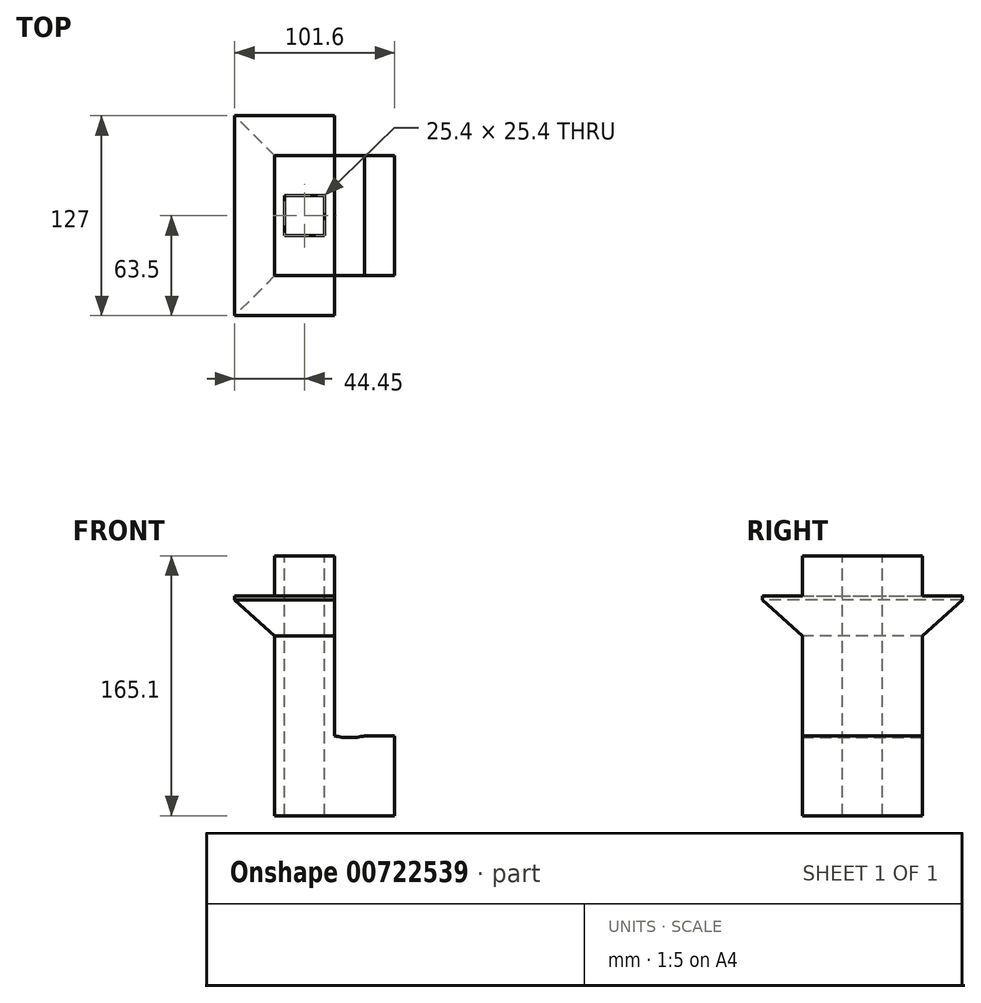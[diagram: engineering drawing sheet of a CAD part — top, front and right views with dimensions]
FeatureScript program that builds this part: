
annotation { "Feature Type Name" : "Feature", "Feature Type Description" : "" }
export const myFeature = defineFeature(function(context is Context, id is Id, definition is map)
    precondition{}
    {
        {
            var Q0;
            Q0=qCreatedBy(makeId("Top.planeOp"),FACE);
            var sketch = newSketch(context, id + "F0", { "sketchPlane" : qUnion([Q0])});
            skLineSegment(sketch, "E0.bottom", {"start": v(19.05, -38.1) * mm, "end": v(-19.05, -38.1) * mm});
            skLineSegment(sketch, "E0.top", {"start": v(19.05, 38.1) * mm, "end": v(-19.05, 38.1) * mm});
            skLineSegment(sketch, "E0.left", {"start": v(19.05, -38.1) * mm, "end": v(19.05, 38.1) * mm});
            skLineSegment(sketch, "E0.right", {"start": v(-19.05, -38.1) * mm, "end": v(-19.05, 38.1) * mm});
            skPoint(sketch, "E0.middle", {"position": v(0, 0) * mm});
            skSolve(sketch);
        }
        {
            var Q0;
            Q0=makeQuery(id+"F0.imprint","IMPRINT",FACE,{"disambiguationData":[TD([[makeQuery(id+"F0.imprint","IMPRINT",EDGE,{"derivedFrom":sQuery(id+"F0.wireOp",EDGE,"E0.bottom")}),-1.0]])]});
            extrude(context, id + "F1", {"entities" : qUnion([Q0]), "depth" : 177.8 * mm, "offsetDistance" : 25.4 * mm});
        }
        {
            var Q0;
            Q0=makeQuery(id+"F1.opExtrude","SWEPT_FACE",FACE,{"disambiguationData":[OSD([sQuery(id+"F0.wireOp",EDGE,"E0.right")])]});
            var sketch = newSketch(context, id + "F2", { "sketchPlane" : qUnion([Q0])});
            skLineSegment(sketch, "E1", {"start": v(38.1, 139.7) * mm, "end": v(-38.1, 139.7) * mm});
            skLineSegment(sketch, "E2", {"start": v(-38.1, 139.7) * mm, "end": v(-38.1, 114.3) * mm});
            skLineSegment(sketch, "E3", {"start": v(-38.1, 114.3) * mm, "end": v(38.1, 114.3) * mm});
            skLineSegment(sketch, "E4", {"start": v(38.1, 114.3) * mm, "end": v(38.1, 139.7) * mm});
            skSolve(sketch);
        }
        {
            var Q0;
            Q0=makeQuery(id+"F2.imprint","IMPRINT",FACE,{"disambiguationData":[TD([[makeQuery(id+"F2.imprint","IMPRINT",EDGE,{"derivedFrom":sQuery(id+"F2.wireOp",EDGE,"E1")}),1.0]])]});
            extrude(context, id + "F3", {"entities" : qUnion([Q0]), "operationType" : NewBodyOperationType.ADD, "depth" : 25.4 * mm, "offsetDistance" : 25.4 * mm});
        }
        {
            var Q0;
            Q0=makeQuery(id+"F3.boolean.opBoolean","MERGE",FACE,{"derivedFrom":[makeQuery(id+"F1.opExtrude","SWEPT_FACE",FACE,{"disambiguationData":[OSD([sQuery(id+"F0.wireOp",EDGE,"E0.bottom")])]}),makeQuery(id+"F3.opExtrude","SWEPT_FACE",FACE,{"disambiguationData":[OSD([sQuery(id+"F2.wireOp",EDGE,"E4")])]})]});
            var sketch = newSketch(context, id + "F4", { "sketchPlane" : qUnion([Q0])});
            skLineSegment(sketch, "E5", {"start": v(-63.5, 114.3) * mm, "end": v(19.05, 114.3) * mm});
            skLineSegment(sketch, "E6", {"start": v(19.05, 114.3) * mm, "end": v(19.05, 139.7) * mm});
            skLineSegment(sketch, "E7", {"start": v(19.05, 139.7) * mm, "end": v(-44.45, 139.7) * mm});
            skSolve(sketch);
        }
        {
            var Q0;
            {var subQ11=sQuery(id+"F4.wireOp",EDGE,"E6");Q0=makeQuery(id+"F4.imprint","IMPRINT",FACE,{"disambiguationData":[TD([[makeQuery(id+"F4.imprint","IMPRINT",EDGE,{"derivedFrom":subQ11}),-1.0]])]});}
            extrude(context, id + "F5", {"entities" : qUnion([Q0]), "operationType" : NewBodyOperationType.ADD, "depth" : 25.4 * mm, "offsetDistance" : 25.4 * mm});
        }
        {
            var Q0;
            Q0=makeQuery(id+"F3.boolean.opBoolean","MERGE",FACE,{"derivedFrom":[makeQuery(id+"F1.opExtrude","SWEPT_FACE",FACE,{"disambiguationData":[OSD([sQuery(id+"F0.wireOp",EDGE,"E0.top")])]}),makeQuery(id+"F3.opExtrude","SWEPT_FACE",FACE,{"disambiguationData":[OSD([sQuery(id+"F2.wireOp",EDGE,"E2")])]})]});
            var sketch = newSketch(context, id + "F6", { "sketchPlane" : qUnion([Q0])});
            skLineSegment(sketch, "E8", {"start": v(44.45, 139.7) * mm, "end": v(-19.05, 139.7) * mm});
            skLineSegment(sketch, "E9", {"start": v(-19.05, 139.7) * mm, "end": v(-19.05, 114.3) * mm});
            skLineSegment(sketch, "E10", {"start": v(-19.05, 114.3) * mm, "end": v(44.45, 114.3) * mm});
            skSolve(sketch);
        }
        {
            var Q0;
            Q0=qSketchRegion(id+"F6",true);
            var Q1;
            {var subQ11=sQuery(id+"F6.wireOp",EDGE,"E9");Q1=makeQuery(id+"F6.imprint","IMPRINT",FACE,{"disambiguationData":[TD([[makeQuery(id+"F6.imprint","IMPRINT",EDGE,{"derivedFrom":subQ11}),1.0]])]});}
            extrude(context, id + "F7", {"entities" : qUnion([Q0, Q1]), "operationType" : NewBodyOperationType.ADD, "depth" : 25.4 * mm, "offsetDistance" : 25.4 * mm});
        }
        {
            var Q0;
            Q0=makeQuery(id+"F7.boolean.opBoolean","MERGE",FACE,{"derivedFrom":[makeQuery(id+"F5.boolean.opBoolean","MERGE",FACE,{"derivedFrom":[makeQuery(id+"F1.opExtrude","SWEPT_FACE",FACE,{"disambiguationData":[OSD([sQuery(id+"F0.wireOp",EDGE,"E0.left")])]}),makeQuery(id+"F5.opExtrude","SWEPT_FACE",FACE,{"disambiguationData":[OSD([sQuery(id+"F4.wireOp",EDGE,"E6")])]})]}),makeQuery(id+"F7.opExtrude","SWEPT_FACE",FACE,{"disambiguationData":[OSD([sQuery(id+"F6.wireOp",EDGE,"E9")])]})]});
            var sketch = newSketch(context, id + "F8", { "sketchPlane" : qUnion([Q0])});
            skLineSegment(sketch, "E11", {"start": v(-63.5, 139.7) * mm, "end": v(-63.5, 137.16) * mm});
            skLineSegment(sketch, "E12", {"start": v(-63.5, 137.16) * mm, "end": v(-38.1, 114.3) * mm});
            skLineSegment(sketch, "E13", {"start": v(63.5, 139.7) * mm, "end": v(63.5, 137.16) * mm});
            skLineSegment(sketch, "E14", {"start": v(63.5, 137.16) * mm, "end": v(38.1, 114.3) * mm});
            skSolve(sketch);
        }
        {
            var Q0;
            Q0=qSketchRegion(id+"F8",true);
            var Q1;
            {var subQ0=sQuery(id+"F8.wireOp",EDGE,"E12");Q1=makeQuery(id+"F8.imprint","IMPRINT",FACE,{"disambiguationData":[TD([[makeQuery(id+"F8.imprint","IMPRINT",EDGE,{"derivedFrom":subQ0}),-1.0]])]});}
            var Q2;
            {var subQ0=sQuery(id+"F8.wireOp",EDGE,"E14");Q2=makeQuery(id+"F8.imprint","IMPRINT",FACE,{"disambiguationData":[TD([[makeQuery(id+"F8.imprint","IMPRINT",EDGE,{"derivedFrom":subQ0}),1.0]])]});}
            extrude(context, id + "F9", {"entities" : qUnion([Q0, Q1, Q2]), "operationType" : NewBodyOperationType.REMOVE, "oppositeDirection" : true, "depth" : 228.6 * mm, "offsetDistance" : 25.4 * mm});
        }
        {
            var Q0;
            Q0=makeQuery(id+"F5.opExtrude","CAP_FACE",FACE,{"disambiguationData":[OSD([sQuery(id+"F2.wireOp",EDGE,"E4"),sQuery(id+"F4.wireOp",EDGE,"E5"),sQuery(id+"F4.wireOp",EDGE,"E6"),sQuery(id+"F4.wireOp",EDGE,"E7")])],"isStart":false});
            var sketch = newSketch(context, id + "F10", { "sketchPlane" : qUnion([Q0])});
            skLineSegment(sketch, "E15", {"start": v(-44.45, 139.7) * mm, "end": v(-44.45, 137.16) * mm});
            skLineSegment(sketch, "E16", {"start": v(-44.45, 139.7) * mm, "end": v(-19.05, 139.7) * mm});
            skLineSegment(sketch, "E17", {"start": v(-19.05, 139.7) * mm, "end": v(-19.05, 114.3) * mm});
            skLineSegment(sketch, "E18", {"start": v(-19.05, 114.3) * mm, "end": v(-44.45, 137.16) * mm});
            skLineSegment(sketch, "E19", {"start": v(-44.45, 137.16) * mm, "end": v(-44.45, 114.3) * mm});
            skLineSegment(sketch, "E20", {"start": v(-44.45, 114.3) * mm, "end": v(-19.05, 114.3) * mm});
            skSolve(sketch);
        }
        {
            var Q0;
            Q0=makeQuery(id+"F10.imprint","IMPRINT",FACE,{"disambiguationData":[TD([[makeQuery(id+"F10.imprint","IMPRINT",EDGE,{"derivedFrom":sQuery(id+"F10.wireOp",EDGE,"E18")}),1.0]])]});
            extrude(context, id + "F11", {"entities" : qUnion([Q0]), "operationType" : NewBodyOperationType.REMOVE, "oppositeDirection" : true, "depth" : 228.6 * mm, "offsetDistance" : 25.4 * mm});
        }
        {
            var Q0;
            Q0=makeQuery(id+"F1.opExtrude","CAP_FACE",FACE,{"disambiguationData":[OSD([sQuery(id+"F0.wireOp",EDGE,"E0.bottom"),sQuery(id+"F0.wireOp",EDGE,"E0.top"),sQuery(id+"F0.wireOp",EDGE,"E0.left"),sQuery(id+"F0.wireOp",EDGE,"E0.right")])],"isStart":false});
            var sketch = newSketch(context, id + "F12", { "sketchPlane" : qUnion([Q0])});
            skLineSegment(sketch, "E21.bottom", {"start": v(-19.05, 38.1) * mm, "end": v(19.05, 38.1) * mm});
            skLineSegment(sketch, "E21.top", {"start": v(-19.05, -38.1) * mm, "end": v(19.05, -38.1) * mm});
            skLineSegment(sketch, "E21.left", {"start": v(-19.05, 38.1) * mm, "end": v(-19.05, -38.1) * mm});
            skLineSegment(sketch, "E21.right", {"start": v(19.05, 38.1) * mm, "end": v(19.05, -38.1) * mm});
            skSolve(sketch);
        }
        {
            var Q0;
            Q0=makeQuery(id+"F12.imprint","IMPRINT",FACE,{"disambiguationData":[TD([[makeQuery(id+"F12.imprint","IMPRINT",EDGE,{"derivedFrom":sQuery(id+"F12.wireOp",EDGE,"E21.bottom")}),1.0]])]});
            extrude(context, id + "F13", {"entities" : qUnion([Q0]), "operationType" : NewBodyOperationType.ADD, "depth" : 25.4 * mm, "offsetDistance" : 25.4 * mm});
        }
        {
            var Q0;
            Q0=makeQuery(id+"F13.opExtrude","CAP_FACE",FACE,{"disambiguationData":[OSD([sQuery(id+"F12.wireOp",EDGE,"E21.bottom"),sQuery(id+"F12.wireOp",EDGE,"E21.top"),sQuery(id+"F12.wireOp",EDGE,"E21.left"),sQuery(id+"F12.wireOp",EDGE,"E21.right")])],"isStart":false});
            var sketch = newSketch(context, id + "F14", { "sketchPlane" : qUnion([Q0])});
            skLineSegment(sketch, "E22", {"start": v(-12.7, 12.7) * mm, "end": v(-12.7, -12.7) * mm});
            skLineSegment(sketch, "E23", {"start": v(-12.7, -12.7) * mm, "end": v(12.7, -12.7) * mm});
            skLineSegment(sketch, "E24", {"start": v(12.7, -12.7) * mm, "end": v(12.7, 12.7) * mm});
            skLineSegment(sketch, "E25", {"start": v(12.7, 12.7) * mm, "end": v(-12.7, 12.7) * mm});
            skSolve(sketch);
        }
        {
            var Q0;
            Q0=qSketchRegion(id+"F14",true);
            extrude(context, id + "F15", {"entities" : qUnion([Q0]), "operationType" : NewBodyOperationType.REMOVE, "oppositeDirection" : true, "depth" : 228.6 * mm, "offsetDistance" : 25.4 * mm});
        }
        {
            var Q0;
            Q0=makeQuery(id+"F13.boolean.opBoolean","MERGE",FACE,{"derivedFrom":[makeQuery(id+"F7.boolean.opBoolean","MERGE",FACE,{"derivedFrom":[makeQuery(id+"F5.boolean.opBoolean","MERGE",FACE,{"derivedFrom":[makeQuery(id+"F1.opExtrude","SWEPT_FACE",FACE,{"disambiguationData":[OSD([sQuery(id+"F0.wireOp",EDGE,"E0.left")])]}),makeQuery(id+"F5.opExtrude","SWEPT_FACE",FACE,{"disambiguationData":[OSD([sQuery(id+"F4.wireOp",EDGE,"E6")])]})]}),makeQuery(id+"F7.opExtrude","SWEPT_FACE",FACE,{"disambiguationData":[OSD([sQuery(id+"F6.wireOp",EDGE,"E9")])]})]}),makeQuery(id+"F13.opExtrude","SWEPT_FACE",FACE,{"disambiguationData":[OSD([sQuery(id+"F12.wireOp",EDGE,"E21.right")])]})]});
            var sketch = newSketch(context, id + "F16", { "sketchPlane" : qUnion([Q0])});
            skLineSegment(sketch, "E26", {"start": v(-38.1, 0) * mm, "end": v(-38.1, 50.8) * mm});
            skLineSegment(sketch, "E27", {"start": v(-38.1, 50.8) * mm, "end": v(38.1, 50.8) * mm});
            skLineSegment(sketch, "E28", {"start": v(38.1, 50.8) * mm, "end": v(38.1, 0) * mm});
            skLineSegment(sketch, "E29", {"start": v(38.1, 0) * mm, "end": v(-38.1, 0) * mm});
            skSolve(sketch);
        }
        {
            var Q0;
            Q0=makeQuery(id+"F16.imprint","IMPRINT",FACE,{"disambiguationData":[TD([[makeQuery(id+"F16.imprint","IMPRINT",EDGE,{"derivedFrom":sQuery(id+"F16.wireOp",EDGE,"E26")}),1.0]])]});
            extrude(context, id + "F17", {"entities" : qUnion([Q0]), "operationType" : NewBodyOperationType.ADD, "depth" : 38.1 * mm, "offsetDistance" : 25.4 * mm});
        }
        {
            var Q0;
            {var subQ2=sQuery(id+"F0.wireOp",EDGE,"E0.bottom");Q0=makeQuery(id+"F17.boolean.opBoolean","MERGE",FACE,{"derivedFrom":[makeQuery(id+"F5.boolean.opBoolean","SPLIT",FACE,{"disambiguationData":[TD([makeQuery(id+"F3.opExtrude","SWEPT_FACE",FACE,{"disambiguationData":[OSD([sQuery(id+"F2.wireOp",EDGE,"E3")])]})])],"derivedFrom":makeQuery(id+"F3.boolean.opBoolean","MERGE",FACE,{"derivedFrom":[makeQuery(id+"F1.opExtrude","SWEPT_FACE",FACE,{"disambiguationData":[OSD([subQ2])]}),makeQuery(id+"F3.opExtrude","SWEPT_FACE",FACE,{"disambiguationData":[OSD([sQuery(id+"F2.wireOp",EDGE,"E4")])]})]})}),makeQuery(id+"F17.opExtrude","SWEPT_FACE",FACE,{"disambiguationData":[OSD([sQuery(id+"F16.wireOp",EDGE,"E26")])]})]});}
            var sketch = newSketch(context, id + "F18", { "sketchPlane" : qUnion([Q0])});
            skArc(sketch, "E30", {"start": v(19.05, 50.8) * mm, "mid": v(28.58, 49.6) * mm, "end": v(38.1, 50.8) * mm});
            skSolve(sketch);
        }
        {
            var Q0;
            {var subQ0=sQuery(id+"F18.wireOp",EDGE,"E30");Q0=makeQuery(id+"F18.imprint","IMPRINT",FACE,{"disambiguationData":[TD([[makeQuery(id+"F18.imprint","IMPRINT",EDGE,{"derivedFrom":subQ0}),1.0]])]});}
            extrude(context, id + "F19", {"entities" : qUnion([Q0]), "operationType" : NewBodyOperationType.REMOVE, "oppositeDirection" : true, "depth" : 228.6 * mm, "offsetDistance" : 25.4 * mm});
        }
        {
            var Q0;
            Q0=makeQuery(id+"F13.opExtrude","CAP_FACE",FACE,{"disambiguationData":[OSD([sQuery(id+"F12.wireOp",EDGE,"E21.bottom"),sQuery(id+"F12.wireOp",EDGE,"E21.top"),sQuery(id+"F12.wireOp",EDGE,"E21.left"),sQuery(id+"F12.wireOp",EDGE,"E21.right")])],"isStart":false});
            var sketch = newSketch(context, id + "F20", { "sketchPlane" : qUnion([Q0])});
            skLineSegment(sketch, "E31", {"start": v(-19.05, 38.1) * mm, "end": v(19.05, 38.1) * mm});
            skLineSegment(sketch, "E32", {"start": v(19.05, 38.1) * mm, "end": v(19.05, -38.1) * mm});
            skLineSegment(sketch, "E33", {"start": v(19.05, -38.1) * mm, "end": v(-19.05, -38.1) * mm});
            skLineSegment(sketch, "E34", {"start": v(-19.05, -38.1) * mm, "end": v(-19.05, 38.1) * mm});
            skSolve(sketch);
        }
        {
            var Q0;
            Q0=makeQuery(id+"F20.imprint","IMPRINT",FACE,{"disambiguationData":[TD([[makeQuery(id+"F20.imprint","IMPRINT",EDGE,{"derivedFrom":sQuery(id+"F20.wireOp",EDGE,"E31")}),1.0]])]});
            extrude(context, id + "F21", {"entities" : qUnion([Q0]), "operationType" : NewBodyOperationType.REMOVE, "oppositeDirection" : true, "depth" : 38.1 * mm, "offsetDistance" : 25.4 * mm});
        }
    });
